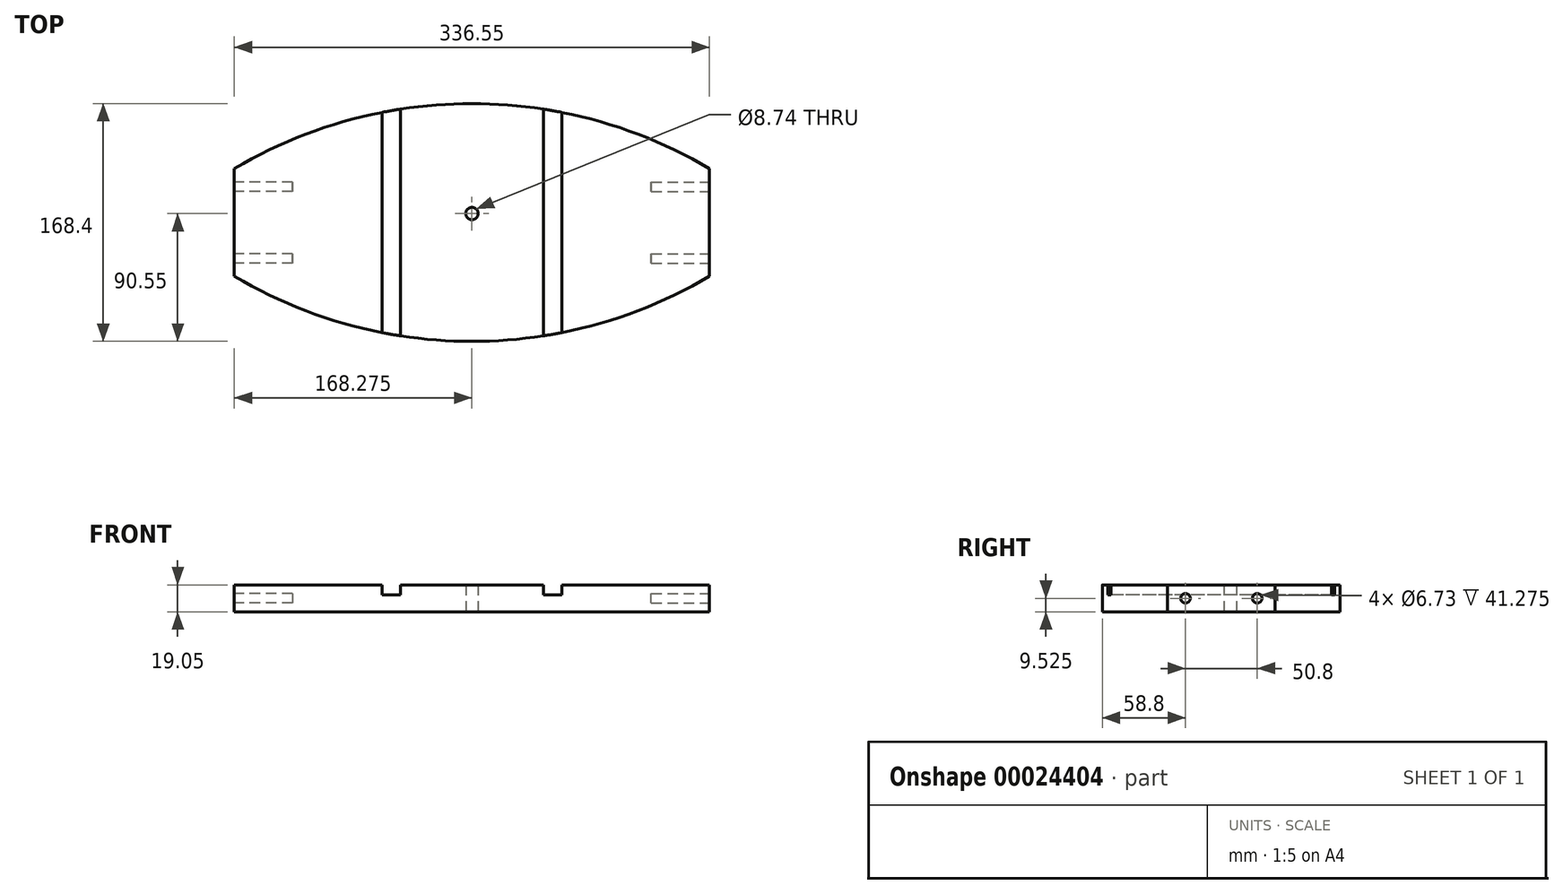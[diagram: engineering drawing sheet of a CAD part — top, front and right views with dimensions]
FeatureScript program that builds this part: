
annotation { "Feature Type Name" : "Feature", "Feature Type Description" : "" }
export const myFeature = defineFeature(function(context is Context, id is Id, definition is map)
    precondition{}
    {
        {
            var Q0;
            Q0=qCreatedBy(makeId("Top.planeOp"),FACE);
            var sketch = newSketch(context, id + "F0", { "sketchPlane" : qUnion([Q0])});
            skLineSegment(sketch, "E0.bottom", {"start": v(0, 0) * mm, "end": v(336.55, 0) * mm, "construction": true});
            skLineSegment(sketch, "E0.top", {"start": v(0, 76.2) * mm, "end": v(336.55, 76.2) * mm, "construction": true});
            skLineSegment(sketch, "E0.left", {"start": v(0, 0) * mm, "end": v(0, 76.2) * mm});
            skLineSegment(sketch, "E0.right", {"start": v(336.55, 0) * mm, "end": v(336.55, 76.2) * mm});
            skArc(sketch, "E1", {"start": v(336.55, 76.2) * mm, "mid": v(168.27, 122.3) * mm, "end": v(0, 76.2) * mm});
            skArc(sketch, "E2", {"start": v(0, 0) * mm, "mid": v(168.28, -46.1) * mm, "end": v(336.55, 0) * mm});
            skLineSegment(sketch, "E3", {"start": v(168.28, 0) * mm, "end": v(168.28, 76.2) * mm, "construction": true});
            skCircle(sketch, "E4", {"center": v(168.28, 44.45) * mm, "radius": 4.37 * mm});
            skSolve(sketch);
        }
        {
            var Q0;
            Q0 = qSketchRegion(id + "F0", true);
            extrude(context, id + "F1", {"entities" : qUnion([Q0]), "depth" : 19.05 * mm});
        }
        {
            var Q0;
            Q0=makeQuery(id+"F1.opExtrude","CAP_FACE",FACE,{"disambiguationData":[OSD([sQuery(id+"F0.wireOp",EDGE,"E0.left"),sQuery(id+"F0.wireOp",EDGE,"E0.right"),sQuery(id+"F0.wireOp",EDGE,"E1"),sQuery(id+"F0.wireOp",EDGE,"E2"),sQuery(id+"F0.wireOp",EDGE,"E4")])],"isStart":false});
            var sketch = newSketch(context, id + "F2", { "sketchPlane" : qUnion([Q0])});
            skLineSegment(sketch, "E5.bottom", {"start": v(104.52, 135.5) * mm, "end": v(117.73, 135.5) * mm});
            skLineSegment(sketch, "E5.top", {"start": v(104.52, -61.17) * mm, "end": v(117.73, -61.17) * mm});
            skLineSegment(sketch, "E5.left", {"start": v(104.52, 135.5) * mm, "end": v(104.52, -61.17) * mm});
            skLineSegment(sketch, "E5.right", {"start": v(117.73, 135.5) * mm, "end": v(117.73, -61.17) * mm});
            skLineSegment(sketch, "E6.bottom", {"start": v(218.82, 137.29) * mm, "end": v(232.03, 137.29) * mm});
            skLineSegment(sketch, "E6.top", {"start": v(218.82, -61.17) * mm, "end": v(232.03, -61.17) * mm});
            skLineSegment(sketch, "E6.left", {"start": v(218.82, 137.29) * mm, "end": v(218.82, -61.17) * mm});
            skLineSegment(sketch, "E6.right", {"start": v(232.03, 137.29) * mm, "end": v(232.03, -61.17) * mm});
            skLineSegment(sketch, "E7", {"start": v(111.12, 135.5) * mm, "end": v(111.12, -61.17) * mm, "construction": true});
            skLineSegment(sketch, "E8", {"start": v(225.43, 137.29) * mm, "end": v(225.43, -61.17) * mm, "construction": true});
            skLineSegment(sketch, "E9", {"start": v(0, 38.1) * mm, "end": v(336.55, 38.1) * mm, "construction": true});
            skLineSegment(sketch, "E10", {"start": v(168.28, 38.1) * mm, "end": v(168.28, -46.1) * mm, "construction": true});
            skSolve(sketch);
        }
        {
            var Q0;
            Q0 = qSketchRegion(id + "F2", true);
            extrude(context, id + "F3", {"entities" : qUnion([Q0]), "operationType" : NewBodyOperationType.REMOVE, "oppositeDirection" : true, "depth" : 7.11 * mm});
        }
        {
            var Q0;
            Q0=makeQuery(id+"F1.opExtrude","SWEPT_FACE",FACE,{"disambiguationData":[OSD([sQuery(id+"F0.wireOp",EDGE,"E0.right")])]});
            var sketch = newSketch(context, id + "F4", { "sketchPlane" : qUnion([Q0])});
            skLineSegment(sketch, "E11", {"start": v(0, 9.53) * mm, "end": v(76.2, 9.53) * mm, "construction": true});
            skLineSegment(sketch, "E12", {"start": v(38.1, 9.53) * mm, "end": v(38.1, 0) * mm, "construction": true});
            skCircle(sketch, "E13", {"center": v(63.5, 9.53) * mm, "radius": 3.37 * mm});
            skCircle(sketch, "E14", {"center": v(12.7, 9.52) * mm, "radius": 3.37 * mm});
            skSolve(sketch);
        }
        {
            var Q0;
            Q0=makeQuery(id+"F4.imprint","IMPRINT",FACE,{"disambiguationData":[TD([[makeQuery(id+"F4.imprint","IMPRINT",EDGE,{"derivedFrom":sQuery(id+"F4.wireOp",EDGE,"E14")}),1.0]])]});
            var Q1;
            Q1=makeQuery(id+"F4.imprint","IMPRINT",FACE,{"disambiguationData":[TD([[makeQuery(id+"F4.imprint","IMPRINT",EDGE,{"derivedFrom":sQuery(id+"F4.wireOp",EDGE,"E13")}),1.0]])]});
            extrude(context, id + "F5", {"entities" : qUnion([Q0, Q1]), "operationType" : NewBodyOperationType.REMOVE, "oppositeDirection" : true, "depth" : 41.27 * mm});
        }
        {
            var Q0;
            Q0=makeQuery(id+"F1.opExtrude","SWEPT_FACE",FACE,{"disambiguationData":[OSD([sQuery(id+"F0.wireOp",EDGE,"E0.left")])]});
            var sketch = newSketch(context, id + "F6", { "sketchPlane" : qUnion([Q0])});
            skLineSegment(sketch, "E15", {"start": v(0, 9.53) * mm, "end": v(-76.2, 9.53) * mm, "construction": true});
            skLineSegment(sketch, "E16", {"start": v(-38.1, 9.53) * mm, "end": v(-38.1, 0) * mm, "construction": true});
            skCircle(sketch, "E17", {"center": v(-63.5, 9.52) * mm, "radius": 3.37 * mm});
            skCircle(sketch, "E18", {"center": v(-12.7, 9.53) * mm, "radius": 3.37 * mm});
            skSolve(sketch);
        }
        {
            var Q0;
            Q0=makeQuery(id+"F6.imprint","IMPRINT",FACE,{"disambiguationData":[TD([[makeQuery(id+"F6.imprint","IMPRINT",EDGE,{"derivedFrom":sQuery(id+"F6.wireOp",EDGE,"E17")}),1.0]])]});
            var Q1;
            Q1=makeQuery(id+"F6.imprint","IMPRINT",FACE,{"disambiguationData":[TD([[makeQuery(id+"F6.imprint","IMPRINT",EDGE,{"derivedFrom":sQuery(id+"F6.wireOp",EDGE,"E18")}),1.0]])]});
            var Q2;
            Q2=sQuery(id+"F6.wireOp",EDGE,"E17");
            var Q3;
            Q3=sQuery(id+"F6.wireOp",EDGE,"E18");
            extrude(context, id + "F7", {"entities" : qUnion([Q0, Q1]), "operationType" : NewBodyOperationType.REMOVE, "surfaceEntities" : qUnion([Q2, Q3]), "oppositeDirection" : true, "depth" : 41.27 * mm});
        }
    });
